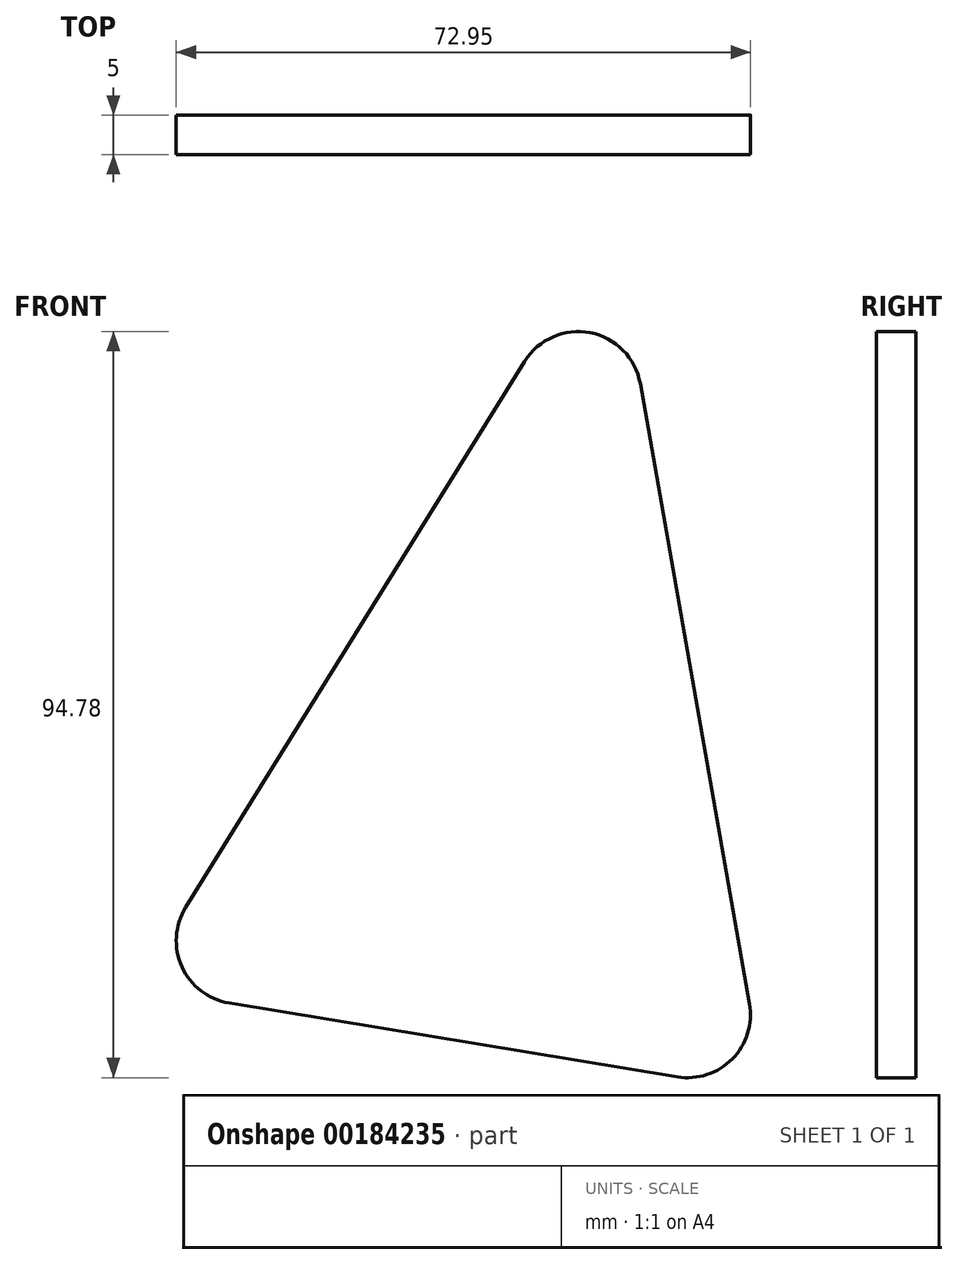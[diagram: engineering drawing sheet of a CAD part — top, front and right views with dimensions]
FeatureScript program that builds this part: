
annotation { "Feature Type Name" : "Feature", "Feature Type Description" : "" }
export const myFeature = defineFeature(function(context is Context, id is Id, definition is map)
    precondition{}
    {
        {
            var Q0;
            Q0=qCreatedBy(makeId("Front.planeOp"),FACE);
            var sketch = newSketch(context, id + "F0", { "sketchPlane" : qUnion([Q0])});
            skCircle(sketch, "E0", {"center": v(0, 0) * mm, "radius": 8 * mm});
            skLineSegment(sketch, "E1", {"start": v(0, 0) * mm, "end": v(50, 0) * mm, "construction": true});
            skLineSegment(sketch, "E2", {"start": v(50, 0) * mm, "end": v(50, 30) * mm, "construction": true});
            skLineSegment(sketch, "E3", {"start": v(50, 30) * mm, "end": v(56.95, -9.4) * mm, "construction": true});
            skLineSegment(sketch, "E4", {"start": v(50, 30) * mm, "end": v(43.05, 69.4) * mm, "construction": true});
            skCircle(sketch, "E5", {"center": v(43.05, 69.4) * mm, "radius": 8 * mm});
            skCircle(sketch, "E6", {"center": v(56.95, -9.4) * mm, "radius": 8 * mm});
            skLineSegment(sketch, "E7", {"start": v(-1.3, -7.9) * mm, "end": v(55.64, -17.29) * mm});
            skLineSegment(sketch, "E8", {"start": v(64.82, -8) * mm, "end": v(50.93, 70.78) * mm});
            skLineSegment(sketch, "E9", {"start": v(-6.8, 4.22) * mm, "end": v(36.26, 73.61) * mm});
            skLineSegment(sketch, "E10", {"start": v(56.95, -9.4) * mm, "end": v(58.34, -17.27) * mm, "construction": true});
            skCircle(sketch, "E11", {"center": v(50, 30) * mm, "radius": 48 * mm, "construction": true});
            skSolve(sketch);
        }
        {
            var Q0;
            {var subQ0=sQuery(id+"F0.wireOp",EDGE,"E7");Q0=makeQuery(id+"F0.imprint","IMPRINT",FACE,{"disambiguationData":[TD([[makeQuery(id+"F0.imprint","IMPRINT",EDGE,{"derivedFrom":subQ0}),1.0]])]});}
            var Q1;
            {var subQ0=sQuery(id+"F0.wireOp",EDGE,"E0");var subQ1=makeQuery(id+"F0.imprint","INTERSECT",VERTEX,{"derivedFrom":[subQ0,sQuery(id+"F0.wireOp",EDGE,"E7")]});Q1=makeQuery(id+"F0.imprint","IMPRINT",FACE,{"disambiguationData":[TD([[makeQuery(id+"F0.imprint","IMPRINT",EDGE,{"disambiguationData":[TD([[subQ1,1.0]])],"derivedFrom":subQ0}),1.0]])]});}
            var Q2;
            {var subQ0=sQuery(id+"F0.wireOp",EDGE,"E6");var subQ1=makeQuery(id+"F0.imprint","INTERSECT",VERTEX,{"derivedFrom":[subQ0,sQuery(id+"F0.wireOp",EDGE,"E7")]});Q2=makeQuery(id+"F0.imprint","IMPRINT",FACE,{"disambiguationData":[TD([[makeQuery(id+"F0.imprint","IMPRINT",EDGE,{"disambiguationData":[TD([[subQ1,-1.0]])],"derivedFrom":subQ0}),1.0]])]});}
            var Q3;
            {var subQ0=sQuery(id+"F0.wireOp",EDGE,"E5");var subQ1=makeQuery(id+"F0.imprint","INTERSECT",VERTEX,{"derivedFrom":[subQ0,sQuery(id+"F0.wireOp",EDGE,"E8")]});Q3=makeQuery(id+"F0.imprint","IMPRINT",FACE,{"disambiguationData":[TD([[makeQuery(id+"F0.imprint","IMPRINT",EDGE,{"disambiguationData":[TD([[subQ1,1.0]])],"derivedFrom":subQ0}),1.0]])]});}
            extrude(context, id + "F1", {"entities" : qUnion([Q0, Q1, Q2, Q3]), "depth" : 5 * mm});
        }
    });
